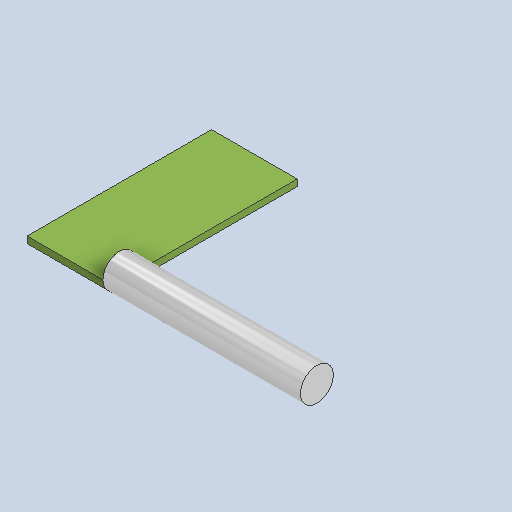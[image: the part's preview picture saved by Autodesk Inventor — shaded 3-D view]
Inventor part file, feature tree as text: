
AUTODESK INVENTOR PART (.ipt)
format: ipt  version: 2025.2 (Build 292293000, 293)  size: 111,104 bytes
history: native  units: mm
features: extrude x2, sketch x2
ambient origin geometry x8: Origin, YZ Plane, XZ Plane, XY Plane, X Axis, Y Axis, Z Axis, Center Point
bodies: Solid1 (feature_tree)
feature tree (4):
  extrude  "Extrusion1"  Depth=28.0mm
  extrude  "Extrusion2"  Depth=30.0mm
  sketch  "Sketch1"  dims[d0=13.0mm d1=28.0mm]
  sketch  "Sketch2"  dims[d2=1.0mm d3=0.0mm d4=0.5mm d5=5.0mm d6=1.0mm d7=30.0mm d8=0.0mm]
